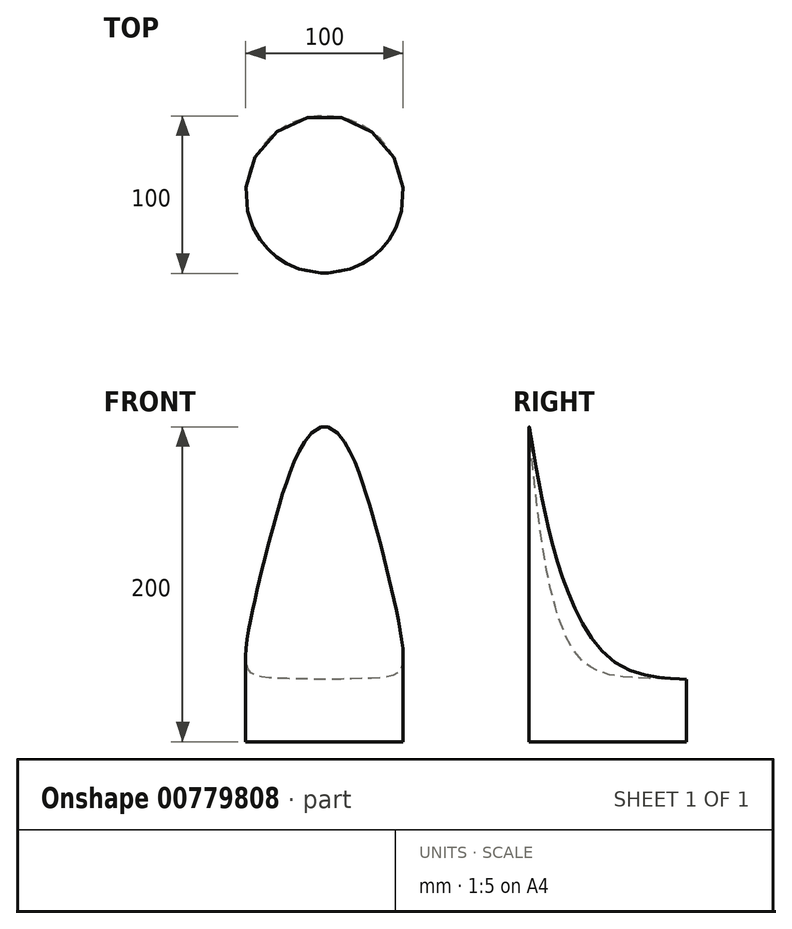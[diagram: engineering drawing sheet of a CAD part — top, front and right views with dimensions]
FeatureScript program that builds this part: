
annotation { "Feature Type Name" : "Feature", "Feature Type Description" : "" }
export const myFeature = defineFeature(function(context is Context, id is Id, definition is map)
    precondition{}
    {
        {
            var Q0;
            Q0=qCreatedBy(makeId("Top.planeOp"),FACE);
            var sketch = newSketch(context, id + "F0", { "sketchPlane" : qUnion([Q0])});
            skCircle(sketch, "E0", {"center": v(0, 0) * mm, "radius": 50 * mm});
            skSolve(sketch);
        }
        {
            var Q0;
            Q0=makeQuery(id+"F0.imprint","IMPRINT",FACE,{"disambiguationData":[TD([[makeQuery(id+"F0.imprint","IMPRINT",EDGE,{"derivedFrom":sQuery(id+"F0.wireOp",EDGE,"E0")}),1.0]])]});
            extrude(context, id + "F1", {"entities" : qUnion([Q0]), "depth" : 200 * mm, "offsetDistance" : 25 * mm});
        }
        {
            var Q0;
            Q0=qCreatedBy(makeId("Right.planeOp"),FACE);
            var sketch = newSketch(context, id + "F2", { "sketchPlane" : qUnion([Q0])});
            skFitSpline(sketch, "E1", {"points": [v(57.37, 39.16) * mm, v(-19.26, 54.65) * mm, v(-50.67, 207.92) * mm], "startDerivative": vector(-300.32, 15.17) * mm, "endDerivative": vector(-27.9, 317.12) * mm});
            skLineSegment(sketch, "E2", {"start": v(57.37, 39.16) * mm, "end": v(57.37, 217.56) * mm});
            skLineSegment(sketch, "E3", {"start": v(-50.67, 207.92) * mm, "end": v(57.37, 217.56) * mm});
            skSolve(sketch);
        }
        {
            var Q0;
            Q0=makeQuery(id+"F2.imprint","IMPRINT",FACE,{"disambiguationData":[TD([[makeQuery(id+"F2.imprint","IMPRINT",EDGE,{"derivedFrom":sQuery(id+"F2.wireOp",EDGE,"E1")}),-1.0]])]});
            var Q1;
            Q1=sQuery(id+"F2.wireOp",EDGE,"E2");
            revolve(context, id + "F3", {"operationType" : NewBodyOperationType.REMOVE, "surfaceOperationType" : NewSurfaceOperationType.NEW, "entities" : qUnion([Q0]), "axis" : qUnion([Q1]), "revolveType" : RevolveType.FULL, "oppositeDirection" : true});
        }
    });
